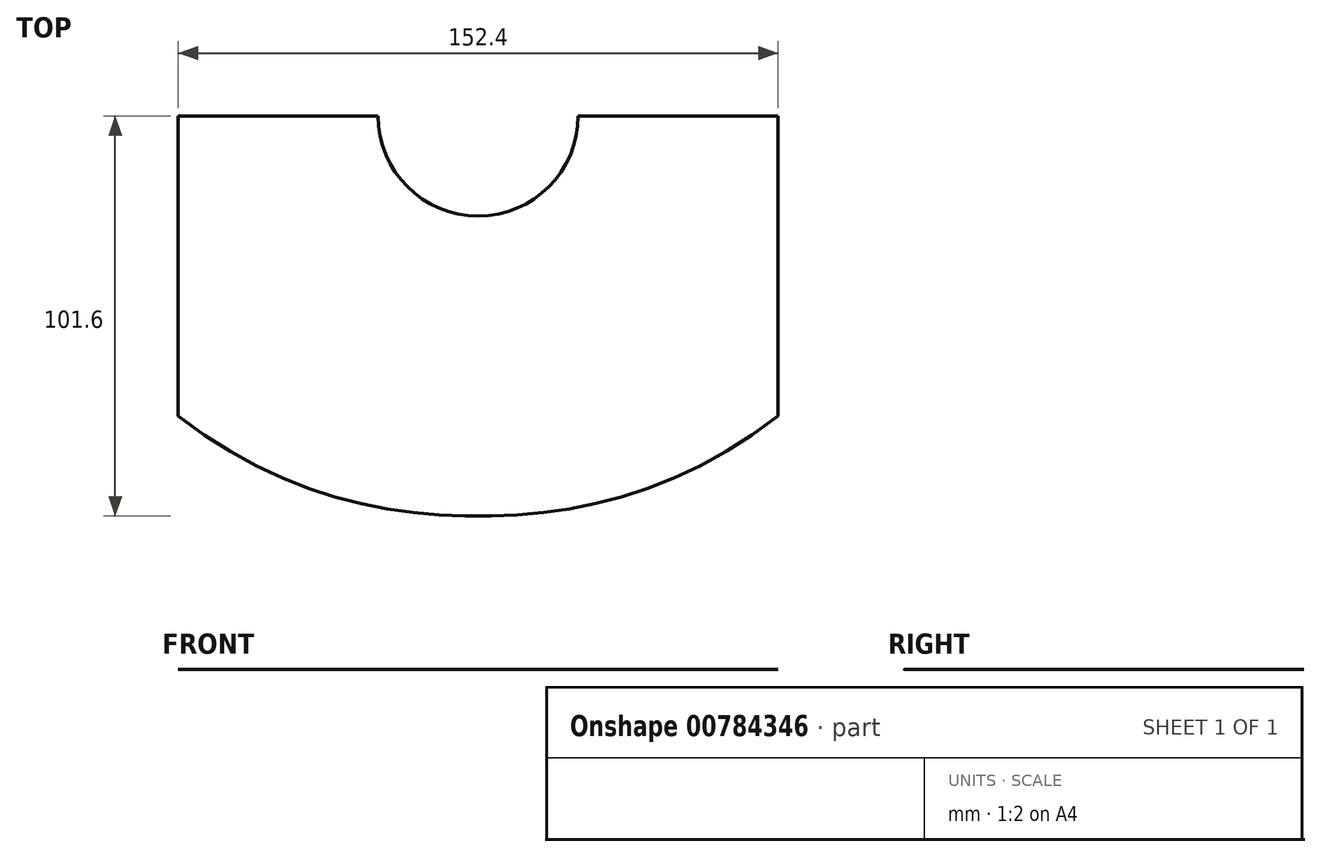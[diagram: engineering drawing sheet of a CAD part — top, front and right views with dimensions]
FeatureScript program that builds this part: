
annotation { "Feature Type Name" : "Feature", "Feature Type Description" : "" }
export const myFeature = defineFeature(function(context is Context, id is Id, definition is map)
    precondition{}
    {
        {
            var Q0;
            Q0=qCreatedBy(makeId("Top.planeOp"),FACE);
            var sketch = newSketch(context, id + "F0", { "sketchPlane" : qUnion([Q0])});
            skLineSegment(sketch, "E0.bottom", {"start": v(-92.9, 42.57) * mm, "end": v(-67.5, 42.57) * mm});
            skLineSegment(sketch, "E0.left", {"start": v(-92.9, 42.57) * mm, "end": v(-92.9, -33.63) * mm});
            skLineSegment(sketch, "E1.bottom", {"start": v(34.1, 42.57) * mm, "end": v(59.5, 42.57) * mm});
            skLineSegment(sketch, "E1.right", {"start": v(59.5, 42.57) * mm, "end": v(59.5, -33.63) * mm});
            skLineSegment(sketch, "E2.bottom", {"start": v(-67.5, 42.57) * mm, "end": v(-42.1, 42.57) * mm});
            skLineSegment(sketch, "E2.right", {"start": v(-42.1, 42.57) * mm, "end": v(-42.1, 42.57) * mm});
            skLineSegment(sketch, "E3.bottom", {"start": v(34.1, 42.57) * mm, "end": v(8.7, 42.57) * mm});
            skLineSegment(sketch, "E3.right", {"start": v(8.7, 42.57) * mm, "end": v(8.7, 42.57) * mm});
            skLineSegment(sketch, "E4", {"start": v(-16.7, 17.17) * mm, "end": v(-16.7, 17.17) * mm});
            skFitSpline(sketch, "E5", {"points": [v(-92.9, -33.63) * mm, v(-16.7, -59.03) * mm, v(59.5, -33.63) * mm], "startDerivative": vector(152.4, -117.7) * mm, "endDerivative": vector(152.4, 117.7) * mm});
            skPoint(sketch, "E6.visualSharp", {"position": v(-42.1, 17.17) * mm});
            skArc(sketch, "E6.filletArc", {"start": v(-42.1, 42.57) * mm, "mid": v(-34.65, 24.6) * mm, "end": v(-16.7, 17.17) * mm});
            skPoint(sketch, "E7.visualSharp", {"position": v(8.7, 17.17) * mm});
            skArc(sketch, "E7.filletArc", {"start": v(-16.7, 17.17) * mm, "mid": v(1.27, 24.6) * mm, "end": v(8.7, 42.57) * mm});
            skSolve(sketch);
        }
        {
            var Q0;
            Q0=makeQuery(id+"F0.imprint","IMPRINT",FACE,{"disambiguationData":[TD([[makeQuery(id+"F0.imprint","IMPRINT",EDGE,{"derivedFrom":sQuery(id+"F0.wireOp",EDGE,"E0.bottom")}),-1.0]])]});
            extrude(context, id + "F1", {"entities" : qUnion([Q0]), "depth" : 1 / 203.2 * mm, "offsetDistance" : 25.4 * mm});
        }
    });
